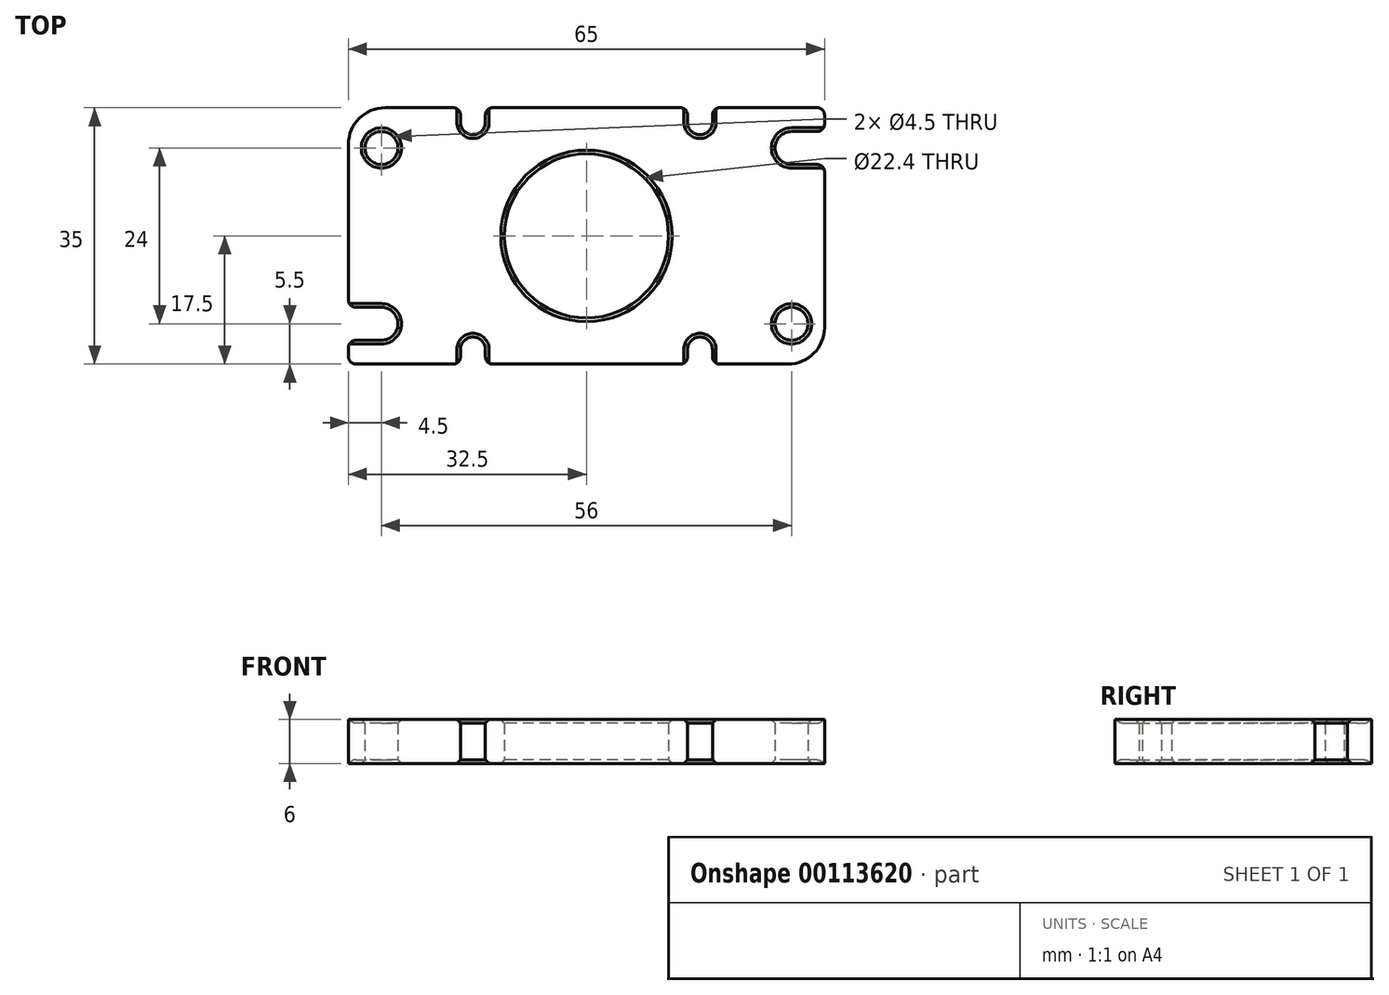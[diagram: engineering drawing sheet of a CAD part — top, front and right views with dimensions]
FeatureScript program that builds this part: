
annotation { "Feature Type Name" : "Feature", "Feature Type Description" : "" }
export const myFeature = defineFeature(function(context is Context, id is Id, definition is map)
    precondition{}
    {
        {
            var Q0;
            Q0=qCreatedBy(makeId("Top.planeOp"),FACE);
            var sketch = newSketch(context, id + "F0", { "sketchPlane" : qUnion([Q0])});
            skLineSegment(sketch, "E0.bottom", {"start": v(-20.65, 20.65) * mm, "end": v(20.65, 20.65) * mm, "construction": true});
            skLineSegment(sketch, "E0.top", {"start": v(-20.65, -20.65) * mm, "end": v(20.65, -20.65) * mm, "construction": true});
            skLineSegment(sketch, "E0.left", {"start": v(-20.65, 20.65) * mm, "end": v(-20.65, -20.65) * mm, "construction": true});
            skLineSegment(sketch, "E0.right", {"start": v(20.65, 20.65) * mm, "end": v(20.65, -20.65) * mm, "construction": true});
            skPoint(sketch, "E0.middle", {"position": v(0, 0) * mm});
            skLineSegment(sketch, "E1.bottom", {"start": v(-15.5, 15.5) * mm, "end": v(15.5, 15.5) * mm, "construction": true});
            skLineSegment(sketch, "E1.top", {"start": v(-15.5, -15.5) * mm, "end": v(15.5, -15.5) * mm, "construction": true});
            skLineSegment(sketch, "E1.left", {"start": v(-15.5, 15.5) * mm, "end": v(-15.5, -15.5) * mm, "construction": true});
            skLineSegment(sketch, "E1.right", {"start": v(15.5, 15.5) * mm, "end": v(15.5, -15.5) * mm, "construction": true});
            skLineSegment(sketch, "E2.bottom", {"start": v(-27.5, 17.5) * mm, "end": v(32.5, 17.5) * mm});
            skLineSegment(sketch, "E2.top", {"start": v(-32.5, -17.5) * mm, "end": v(27.5, -17.5) * mm});
            skLineSegment(sketch, "E2.left", {"start": v(-32.5, 12.5) * mm, "end": v(-32.5, -17.5) * mm});
            skLineSegment(sketch, "E2.right", {"start": v(32.5, 17.5) * mm, "end": v(32.5, -12.5) * mm});
            skCircle(sketch, "E3", {"center": v(0, 0) * mm, "radius": 11.2 * mm});
            skLineSegment(sketch, "E4", {"start": v(-15.5, 15.5) * mm, "end": v(-15.5, 17.5) * mm});
            skLineSegment(sketch, "E5", {"start": v(15.5, 15.5) * mm, "end": v(15.5, 17.5) * mm});
            skLineSegment(sketch, "E6", {"start": v(-15.5, -15.5) * mm, "end": v(-15.5, -17.5) * mm});
            skLineSegment(sketch, "E7", {"start": v(15.5, -15.5) * mm, "end": v(15.5, -17.5) * mm});
            skCircle(sketch, "E8", {"center": v(-28, -12) * mm, "radius": 2.25 * mm});
            skCircle(sketch, "E9", {"center": v(-28, 12) * mm, "radius": 2.25 * mm});
            skCircle(sketch, "E10", {"center": v(28, 12) * mm, "radius": 2.25 * mm});
            skCircle(sketch, "E11", {"center": v(28, -12) * mm, "radius": 2.25 * mm});
            skLineSegment(sketch, "E12", {"start": v(-28, -12) * mm, "end": v(-32.5, -12) * mm, "construction": true});
            skLineSegment(sketch, "E13", {"start": v(28, -12) * mm, "end": v(32.5, -12) * mm, "construction": true});
            skLineSegment(sketch, "E14", {"start": v(28, 12) * mm, "end": v(32.5, 12) * mm, "construction": true});
            skLineSegment(sketch, "E15", {"start": v(32.5, 12) * mm, "end": v(28, 12) * mm, "construction": true});
            skLineSegment(sketch, "E16", {"start": v(-28, 12) * mm, "end": v(-32.5, 12) * mm, "construction": true});
            skPoint(sketch, "E17.visualSharp", {"position": v(-32.5, 17.5) * mm});
            skArc(sketch, "E17.filletArc", {"start": v(-27.5, 17.5) * mm, "mid": v(-31.04, 16.04) * mm, "end": v(-32.5, 12.5) * mm});
            skPoint(sketch, "E18.visualSharp", {"position": v(32.5, -17.5) * mm});
            skArc(sketch, "E18.filletArc", {"start": v(27.5, -17.5) * mm, "mid": v(31.04, -16.04) * mm, "end": v(32.5, -12.5) * mm});
            skLineSegment(sketch, "E19", {"start": v(-28, 12) * mm, "end": v(-28, -24.99) * mm, "construction": true});
            skLineSegment(sketch, "E20", {"start": v(28, 12) * mm, "end": v(28, -26.36) * mm, "construction": true});
            skLineSegment(sketch, "E21", {"start": v(-28, -9.75) * mm, "end": v(-32.5, -9.75) * mm});
            skLineSegment(sketch, "E22", {"start": v(-28, -14.25) * mm, "end": v(-32.5, -14.25) * mm});
            skLineSegment(sketch, "E23", {"start": v(28, 9.75) * mm, "end": v(32.5, 9.75) * mm});
            skLineSegment(sketch, "E24", {"start": v(28, 12) * mm, "end": v(28, 14.25) * mm, "construction": true});
            skLineSegment(sketch, "E25", {"start": v(28, 14.25) * mm, "end": v(32.5, 14.25) * mm});
            skCircle(sketch, "E26", {"center": v(-15.5, 15.5) * mm, "radius": 1.7 * mm});
            skCircle(sketch, "E27", {"center": v(-15.5, -15.5) * mm, "radius": 1.7 * mm});
            skCircle(sketch, "E28", {"center": v(15.5, 15.5) * mm, "radius": 1.7 * mm});
            skCircle(sketch, "E29", {"center": v(15.5, -15.5) * mm, "radius": 1.7 * mm});
            skLineSegment(sketch, "E30", {"start": v(-15.5, -15.5) * mm, "end": v(-17.2, -15.5) * mm, "construction": true});
            skLineSegment(sketch, "E31", {"start": v(-17.2, -15.5) * mm, "end": v(-17.2, -17.5) * mm});
            skLineSegment(sketch, "E32", {"start": v(-13.8, -15.5) * mm, "end": v(-13.8, -17.5) * mm});
            skLineSegment(sketch, "E33", {"start": v(13.8, -15.5) * mm, "end": v(13.8, -17.5) * mm});
            skLineSegment(sketch, "E34", {"start": v(15.5, -15.5) * mm, "end": v(17.2, -15.5) * mm, "construction": true});
            skLineSegment(sketch, "E35", {"start": v(17.2, -15.5) * mm, "end": v(17.2, -17.5) * mm});
            skLineSegment(sketch, "E36", {"start": v(13.8, 15.5) * mm, "end": v(13.8, 17.5) * mm});
            skLineSegment(sketch, "E37", {"start": v(15.5, 15.5) * mm, "end": v(17.2, 15.5) * mm, "construction": true});
            skLineSegment(sketch, "E38", {"start": v(17.2, 15.5) * mm, "end": v(17.2, 17.5) * mm});
            skLineSegment(sketch, "E39", {"start": v(-15.5, 15.5) * mm, "end": v(-17.2, 15.5) * mm, "construction": true});
            skLineSegment(sketch, "E40", {"start": v(-17.2, 15.5) * mm, "end": v(-17.2, 17.5) * mm});
            skLineSegment(sketch, "E41", {"start": v(-13.8, 15.5) * mm, "end": v(-13.8, 17.5) * mm});
            skSolve(sketch);
        }
        {
            var Q0;
            Q0=makeQuery(id+"F0.imprint","IMPRINT",FACE,{"disambiguationData":[TD([[makeQuery(id+"F0.imprint","IMPRINT",EDGE,{"derivedFrom":sQuery(id+"F0.wireOp",EDGE,"E3")}),-1.0]])]});
            extrude(context, id + "F1", {"entities" : qUnion([Q0]), "depth" : 6 * mm});
        }
        {
            var Q0;
            Q0=makeQuery(id+"F1.opExtrude","CAP_EDGE",EDGE,{"disambiguationData":[OSD([sQuery(id+"F0.wireOp",EDGE,"E3")])],"isStart":false});
            var Q1;
            Q1=makeQuery(id+"F1.opExtrude","CAP_EDGE",EDGE,{"disambiguationData":[OSD([sQuery(id+"F0.wireOp",EDGE,"E3")])],"isStart":true});
            var Q2;
            Q2=makeQuery(id+"F1.opExtrude","CAP_EDGE",EDGE,{"disambiguationData":[OSD([sQuery(id+"F0.wireOp",EDGE,"E8")])],"isStart":true});
            var Q3;
            Q3=makeQuery(id+"F1.opExtrude","CAP_EDGE",EDGE,{"disambiguationData":[OSD([sQuery(id+"F0.wireOp",EDGE,"E27")])],"isStart":true});
            var Q4;
            Q4=makeQuery(id+"F1.opExtrude","CAP_EDGE",EDGE,{"disambiguationData":[OSD([sQuery(id+"F0.wireOp",EDGE,"E29")])],"isStart":true});
            var Q5;
            Q5=makeQuery(id+"F1.opExtrude","CAP_EDGE",EDGE,{"disambiguationData":[OSD([sQuery(id+"F0.wireOp",EDGE,"E11")])],"isStart":true});
            var Q6;
            Q6=makeQuery(id+"F1.opExtrude","CAP_EDGE",EDGE,{"disambiguationData":[OSD([sQuery(id+"F0.wireOp",EDGE,"E10")])],"isStart":true});
            var Q7;
            Q7=makeQuery(id+"F1.opExtrude","CAP_EDGE",EDGE,{"disambiguationData":[OSD([sQuery(id+"F0.wireOp",EDGE,"E28")])],"isStart":true});
            var Q8;
            Q8=makeQuery(id+"F1.opExtrude","CAP_EDGE",EDGE,{"disambiguationData":[OSD([sQuery(id+"F0.wireOp",EDGE,"E26")])],"isStart":true});
            var Q9;
            Q9=makeQuery(id+"F1.opExtrude","CAP_EDGE",EDGE,{"disambiguationData":[OSD([sQuery(id+"F0.wireOp",EDGE,"E9")])],"isStart":true});
            var Q10;
            Q10=makeQuery(id+"F1.opExtrude","CAP_EDGE",EDGE,{"disambiguationData":[OSD([sQuery(id+"F0.wireOp",EDGE,"E9")])],"isStart":false});
            var Q11;
            Q11=makeQuery(id+"F1.opExtrude","CAP_EDGE",EDGE,{"disambiguationData":[OSD([sQuery(id+"F0.wireOp",EDGE,"E26")])],"isStart":false});
            var Q12;
            Q12=makeQuery(id+"F1.opExtrude","CAP_EDGE",EDGE,{"disambiguationData":[OSD([sQuery(id+"F0.wireOp",EDGE,"E28")])],"isStart":false});
            var Q13;
            Q13=makeQuery(id+"F1.opExtrude","CAP_EDGE",EDGE,{"disambiguationData":[OSD([sQuery(id+"F0.wireOp",EDGE,"E10")])],"isStart":false});
            var Q14;
            Q14=makeQuery(id+"F1.opExtrude","CAP_EDGE",EDGE,{"disambiguationData":[OSD([sQuery(id+"F0.wireOp",EDGE,"E8")])],"isStart":false});
            var Q15;
            Q15=makeQuery(id+"F1.opExtrude","CAP_EDGE",EDGE,{"disambiguationData":[OSD([sQuery(id+"F0.wireOp",EDGE,"E27")])],"isStart":false});
            var Q16;
            Q16=makeQuery(id+"F1.opExtrude","CAP_EDGE",EDGE,{"disambiguationData":[OSD([sQuery(id+"F0.wireOp",EDGE,"E29")])],"isStart":false});
            var Q17;
            Q17=makeQuery(id+"F1.opExtrude","CAP_EDGE",EDGE,{"disambiguationData":[OSD([sQuery(id+"F0.wireOp",EDGE,"E11")])],"isStart":false});
            chamfer(context, id + "F2", {"entities" : qUnion([Q0, Q1, Q2, Q3, Q4, Q5, Q6, Q7, Q8, Q9, Q10, Q11, Q12, Q13, Q14, Q15, Q16, Q17]), "width" : 0.5 * mm, "tangentPropagation" : true});
        }
        {
            var Q0;
            Q0=makeQuery(id+"F1.opExtrude","SWEPT_EDGE",EDGE,{"disambiguationData":[OSD([sQuery(id+"F0.wireOp",EDGE,"E2.left"),sQuery(id+"F0.wireOp",EDGE,"E22")])]});
            var Q1;
            Q1=makeQuery(id+"F1.opExtrude","SWEPT_EDGE",EDGE,{"disambiguationData":[OSD([sQuery(id+"F0.wireOp",EDGE,"E2.left"),sQuery(id+"F0.wireOp",EDGE,"E21")])]});
            var Q2;
            Q2=makeQuery(id+"F1.opExtrude","SWEPT_EDGE",EDGE,{"disambiguationData":[OSD([sQuery(id+"F0.wireOp",EDGE,"E2.top"),sQuery(id+"F0.wireOp",EDGE,"E2.left")])]});
            var Q3;
            Q3=makeQuery(id+"F1.opExtrude","SWEPT_EDGE",EDGE,{"disambiguationData":[OSD([sQuery(id+"F0.wireOp",EDGE,"E2.top"),sQuery(id+"F0.wireOp",EDGE,"E31")])]});
            var Q4;
            Q4=makeQuery(id+"F1.opExtrude","SWEPT_EDGE",EDGE,{"disambiguationData":[OSD([sQuery(id+"F0.wireOp",EDGE,"E2.top"),sQuery(id+"F0.wireOp",EDGE,"E32")])]});
            var Q5;
            Q5=makeQuery(id+"F1.opExtrude","SWEPT_EDGE",EDGE,{"disambiguationData":[OSD([sQuery(id+"F0.wireOp",EDGE,"E2.top"),sQuery(id+"F0.wireOp",EDGE,"E33")])]});
            var Q6;
            Q6=makeQuery(id+"F1.opExtrude","SWEPT_EDGE",EDGE,{"disambiguationData":[OSD([sQuery(id+"F0.wireOp",EDGE,"E2.top"),sQuery(id+"F0.wireOp",EDGE,"E35")])]});
            var Q7;
            Q7=makeQuery(id+"F1.opExtrude","SWEPT_EDGE",EDGE,{"disambiguationData":[OSD([sQuery(id+"F0.wireOp",EDGE,"E2.right"),sQuery(id+"F0.wireOp",EDGE,"E25")])]});
            var Q8;
            Q8=makeQuery(id+"F1.opExtrude","SWEPT_EDGE",EDGE,{"disambiguationData":[OSD([sQuery(id+"F0.wireOp",EDGE,"E2.right"),sQuery(id+"F0.wireOp",EDGE,"E23")])]});
            var Q9;
            Q9=makeQuery(id+"F1.opExtrude","SWEPT_EDGE",EDGE,{"disambiguationData":[OSD([sQuery(id+"F0.wireOp",EDGE,"E2.bottom"),sQuery(id+"F0.wireOp",EDGE,"E2.right")])]});
            var Q10;
            Q10=makeQuery(id+"F1.opExtrude","SWEPT_EDGE",EDGE,{"disambiguationData":[OSD([sQuery(id+"F0.wireOp",EDGE,"E2.bottom"),sQuery(id+"F0.wireOp",EDGE,"E38")])]});
            var Q11;
            Q11=makeQuery(id+"F1.opExtrude","SWEPT_EDGE",EDGE,{"disambiguationData":[OSD([sQuery(id+"F0.wireOp",EDGE,"E2.bottom"),sQuery(id+"F0.wireOp",EDGE,"E36")])]});
            var Q12;
            Q12=makeQuery(id+"F1.opExtrude","SWEPT_EDGE",EDGE,{"disambiguationData":[OSD([sQuery(id+"F0.wireOp",EDGE,"E2.bottom"),sQuery(id+"F0.wireOp",EDGE,"E41")])]});
            var Q13;
            Q13=makeQuery(id+"F1.opExtrude","SWEPT_EDGE",EDGE,{"disambiguationData":[OSD([sQuery(id+"F0.wireOp",EDGE,"E2.bottom"),sQuery(id+"F0.wireOp",EDGE,"E40")])]});
            fillet(context, id + "F3", {"entities" : qUnion([Q0, Q1, Q2, Q3, Q4, Q5, Q6, Q7, Q8, Q9, Q10, Q11, Q12, Q13]), "radius" : 1 * mm, "tangentPropagation" : true, "allowEdgeOverflow" : false});
        }
    });
